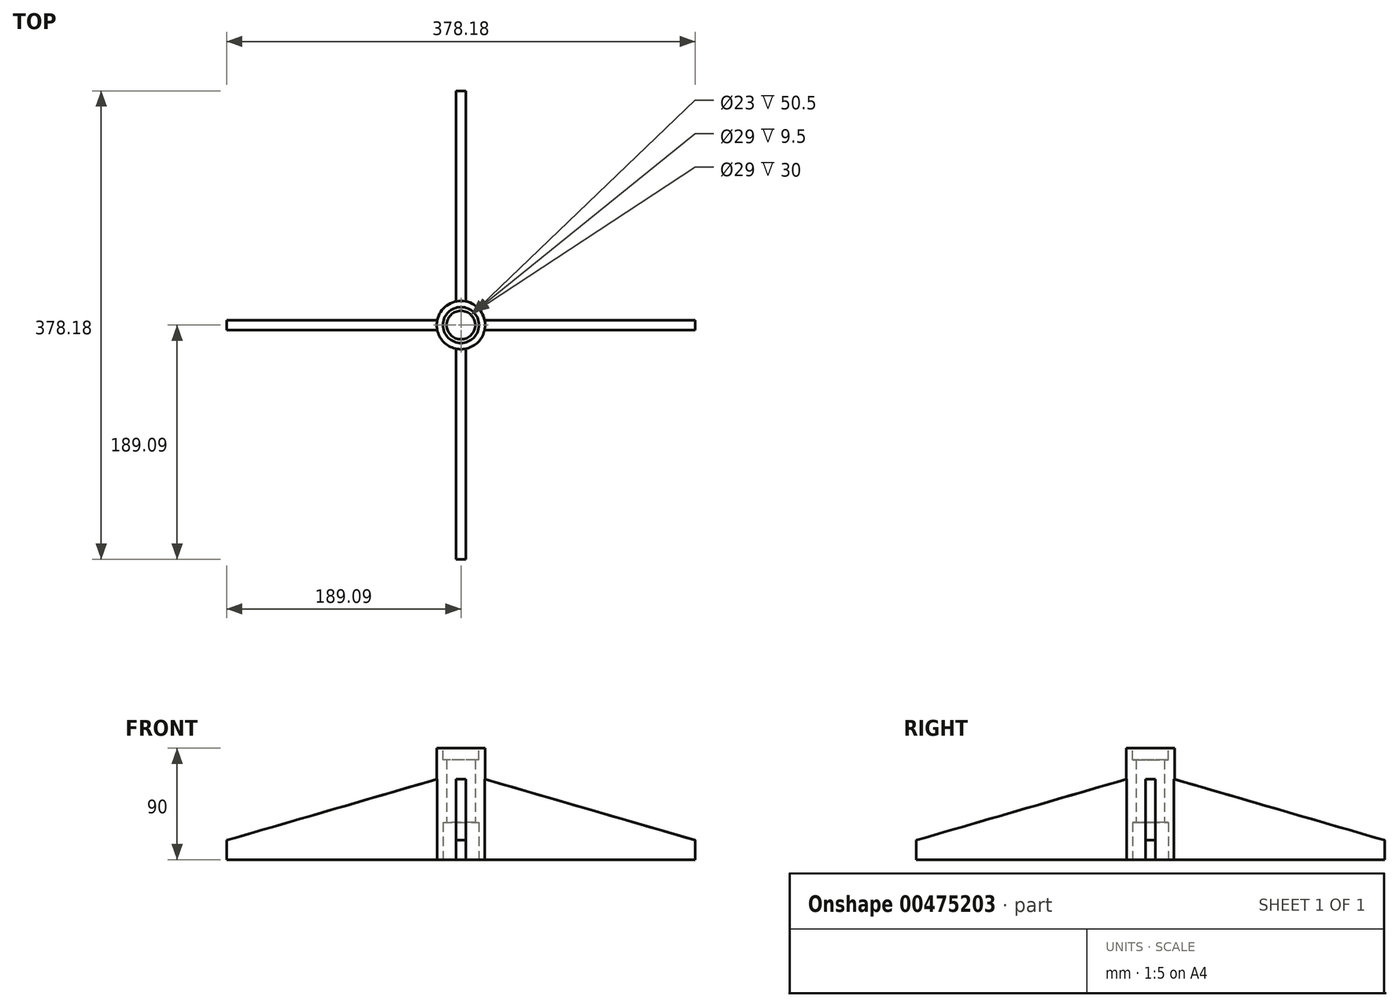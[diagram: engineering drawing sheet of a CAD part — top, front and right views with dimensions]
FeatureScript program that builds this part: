
annotation { "Feature Type Name" : "Feature", "Feature Type Description" : "" }
export const myFeature = defineFeature(function(context is Context, id is Id, definition is map)
    precondition{}
    {
        {
            var Q0;
            Q0=qCreatedBy(makeId("Top.planeOp"),FACE);
            var sketch = newSketch(context, id + "F0", { "sketchPlane" : qUnion([Q0])});
            skCircle(sketch, "E0", {"center": v(0, 0) * mm, "radius": 19.5 * mm});
            skCircle(sketch, "E1", {"center": v(0, 0) * mm, "radius": 11.5 * mm});
            skSolve(sketch);
        }
        {
            var Q0;
            Q0=makeQuery(id+"F0.imprint","IMPRINT",FACE,{"disambiguationData":[TD([[makeQuery(id+"F0.imprint","IMPRINT",EDGE,{"derivedFrom":sQuery(id+"F0.wireOp",EDGE,"E0")}),1.0]])]});
            extrude(context, id + "F1", {"entities" : qUnion([Q0]), "endBound" : BoundingType.SYMMETRIC, "depth" : 90 * mm});
        }
        {
            var Q0;
            Q0=makeQuery(id+"F1.opExtrude","CAP_FACE",FACE,{"disambiguationData":[OSD([sQuery(id+"F0.wireOp",EDGE,"E0"),sQuery(id+"F0.wireOp",EDGE,"E1")])],"isStart":false});
            var sketch = newSketch(context, id + "F2", { "sketchPlane" : qUnion([Q0])});
            skCircle(sketch, "E2", {"center": v(0, 0) * mm, "radius": 14.5 * mm});
            skCircle(sketch, "E3.0", {"center": v(0, 0) * mm, "radius": 11.5 * mm});
            skSolve(sketch);
        }
        {
            var Q0;
            Q0=makeQuery(id+"F2.imprint","IMPRINT",FACE,{"disambiguationData":[TD([[makeQuery(id+"F2.imprint","IMPRINT",EDGE,{"derivedFrom":sQuery(id+"F2.wireOp",EDGE,"E2")}),1.0]])]});
            extrude(context, id + "F3", {"entities" : qUnion([Q0]), "operationType" : NewBodyOperationType.REMOVE, "oppositeDirection" : true, "depth" : 9.5 * mm});
        }
        {
            var Q0;
            Q0=makeQuery(id+"F1.opExtrude","CAP_FACE",FACE,{"disambiguationData":[OSD([sQuery(id+"F0.wireOp",EDGE,"E0"),sQuery(id+"F0.wireOp",EDGE,"E1")])],"isStart":true});
            var sketch = newSketch(context, id + "F4", { "sketchPlane" : qUnion([Q0])});
            skCircle(sketch, "E4", {"center": v(0, 0) * mm, "radius": 14.5 * mm});
            skCircle(sketch, "E5.0", {"center": v(0, 0) * mm, "radius": 11.5 * mm});
            skSolve(sketch);
        }
        {
            var Q0;
            Q0=makeQuery(id+"F4.imprint","IMPRINT",FACE,{"disambiguationData":[TD([[makeQuery(id+"F4.imprint","IMPRINT",EDGE,{"derivedFrom":sQuery(id+"F4.wireOp",EDGE,"E4")}),1.0]])]});
            extrude(context, id + "F5", {"entities" : qUnion([Q0]), "operationType" : NewBodyOperationType.REMOVE, "oppositeDirection" : true, "depth" : 30 * mm});
        }
        {
            var Q0;
            Q0=qCreatedBy(makeId("Right.planeOp"),FACE);
            cPlane(context, id + "F6", {"entities" : qUnion([Q0]), "cplaneType" : CPlaneType.OFFSET, "offset" : 19 * mm, "width" : 150 * mm, "height" : 150 * mm});
        }
        {
            var Q0;
            Q0=qCreatedBy(id+"F6.planeOp",FACE);
            var sketch = newSketch(context, id + "F7", { "sketchPlane" : qUnion([Q0])});
            skLineSegment(sketch, "E6", {"start": v(-4, 20) * mm, "end": v(4, 20) * mm});
            skLineSegment(sketch, "E7", {"start": v(-4, 20) * mm, "end": v(-4, -45) * mm});
            skLineSegment(sketch, "E8", {"start": v(-4, -45) * mm, "end": v(4, -45) * mm});
            skLineSegment(sketch, "E9", {"start": v(4, -45) * mm, "end": v(4, 20) * mm});
            skSolve(sketch);
        }
        {
            var Q0;
            Q0=qCreatedBy(makeId("Right.planeOp"),FACE);
            var sketch = newSketch(context, id + "F8", { "sketchPlane" : qUnion([Q0])});
            skLineSegment(sketch, "E10", {"start": v(0, 61.67) * mm, "end": v(0, -54.72) * mm, "construction": true});
            skSolve(sketch);
        }
        {
            var Q0;
            Q0=qCreatedBy(makeId("Right.planeOp"),FACE);
            var Q1;
            Q1=sQuery(id+"F8.wireOp",EDGE,"E10");
            cPlane(context, id + "F9", {"entities" : qUnion([Q0, Q1]), "cplaneType" : CPlaneType.LINE_ANGLE, "offset" : 25 * mm, "angle" : 120 * degree, "width" : 150 * mm, "height" : 150 * mm});
        }
        {
            var Q0;
            Q0=makeQuery(id+"FmNTNJQfuQ9f8jD_1.boolean.opBoolean","MERGE",FACE,{"derivedFrom":[makeQuery(id+"F1.opExtrude","CAP_FACE",FACE,{"disambiguationData":[OSD([sQuery(id+"F0.wireOp",EDGE,"E0"),sQuery(id+"F0.wireOp",EDGE,"E1")])],"isStart":true}),makeQuery(id+"FmNTNJQfuQ9f8jD_1.opExtrude","SWEPT_FACE",FACE,{"disambiguationData":[OSD([sQuery(id+"F7.wireOp",EDGE,"E8")])]})]});
            var sketch = newSketch(context, id + "F10", { "sketchPlane" : qUnion([Q0])});
            skLineSegment(sketch, "E11.0", {"start": v(189.09, 4) * mm, "end": v(19.09, 4) * mm});
            skLineSegment(sketch, "E12.0", {"start": v(189.09, 4) * mm, "end": v(189.09, -4) * mm});
            skLineSegment(sketch, "E13.0", {"start": v(189.09, -4) * mm, "end": v(19.09, -4) * mm});
            skLineSegment(sketch, "E14", {"start": v(19.09, 4) * mm, "end": v(19.09, -4) * mm});
            skLineSegment(sketch, "E15.1.0", {"start": v(-4, 189.09) * mm, "end": v(-4, 19.09) * mm});
            skLineSegment(sketch, "E15.1.1", {"start": v(4, 189.09) * mm, "end": v(4, 19.09) * mm});
            skLineSegment(sketch, "E15.1.2", {"start": v(-4, 19.09) * mm, "end": v(4, 19.09) * mm});
            skLineSegment(sketch, "E15.1.3", {"start": v(-4, 189.09) * mm, "end": v(4, 189.09) * mm});
            skLineSegment(sketch, "E15.2.0", {"start": v(-189.09, -4) * mm, "end": v(-19.09, -4) * mm});
            skLineSegment(sketch, "E15.2.1", {"start": v(-189.09, 4) * mm, "end": v(-19.09, 4) * mm});
            skLineSegment(sketch, "E15.2.2", {"start": v(-19.09, -4) * mm, "end": v(-19.09, 4) * mm});
            skLineSegment(sketch, "E15.2.3", {"start": v(-189.09, -4) * mm, "end": v(-189.09, 4) * mm});
            skLineSegment(sketch, "E15.3.0", {"start": v(4, -189.09) * mm, "end": v(4, -19.09) * mm});
            skLineSegment(sketch, "E15.3.1", {"start": v(-4, -189.09) * mm, "end": v(-4, -19.09) * mm});
            skLineSegment(sketch, "E15.3.2", {"start": v(4, -19.09) * mm, "end": v(-4, -19.09) * mm});
            skLineSegment(sketch, "E15.3.3", {"start": v(4, -189.09) * mm, "end": v(-4, -189.09) * mm});
            skPoint(sketch, "E15.center", {"position": v(0, 0) * mm});
            skSolve(sketch);
        }
        {
            var Q0;
            Q0=qSketchRegion(id+"F10",true);
            extrude(context, id + "F11", {"entities" : qUnion([Q0]), "operationType" : NewBodyOperationType.ADD, "oppositeDirection" : true, "depth" : 65 * mm});
        }
        {
            var Q0;
            Q0=makeQuery(id+"F11.opExtrude","SWEPT_FACE",FACE,{"disambiguationData":[OSD([sQuery(id+"F10.wireOp",EDGE,"E11.0")])]});
            var sketch = newSketch(context, id + "F12", { "sketchPlane" : qUnion([Q0])});
            skLineSegment(sketch, "E16", {"start": v(19.09, 20) * mm, "end": v(189.09, -29.38) * mm});
            skLineSegment(sketch, "E17", {"start": v(189.09, -29.38) * mm, "end": v(189.09, 20) * mm});
            skLineSegment(sketch, "E18", {"start": v(189.09, 20) * mm, "end": v(19.09, 20) * mm});
            skSolve(sketch);
        }
        {
            var Q0;
            Q0=makeQuery(id+"F12.imprint","IMPRINT",FACE,{"disambiguationData":[TD([[makeQuery(id+"F12.imprint","IMPRINT",EDGE,{"derivedFrom":sQuery(id+"F12.wireOp",EDGE,"E16")}),1.0]])]});
            var Q1;
            Q1=sQuery(id+"F8.wireOp",EDGE,"E10");
            revolve(context, id + "F13", {"operationType" : NewBodyOperationType.REMOVE, "entities" : qUnion([Q0]), "axis" : qUnion([Q1]), "revolveType" : RevolveType.FULL, "oppositeDirection" : true});
        }
    });
